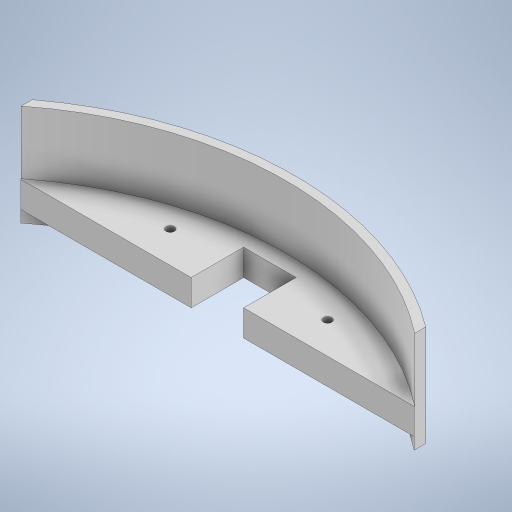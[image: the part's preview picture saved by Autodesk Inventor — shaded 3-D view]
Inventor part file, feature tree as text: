
AUTODESK INVENTOR PART (.ipt)
format: ipt  version: 2023 (Build 270158000, 158)  size: 374,784 bytes
history: native  units: mm
features: sketch x14, extrude x13, other x1, hole x1
ambient origin geometry x8: Origin, YZ Plane, XZ Plane, XY Plane, X Axis, Y Axis, Z Axis, Center Point
bodies: Body1 (feature_tree)
feature tree (29):
  other  "ソリッド1"
  extrude  "押し出し1"  Depth=250.0mm
  extrude  "押し出し2"  Depth=4.0mm TaperAngle=0.0deg
  sketch  "スケッチ4"
  extrude  "押し出し3"  Depth=150.0mm
  extrude  "押し出し4"  Depth=180.0mm
  extrude  "押し出し5"  Depth=243.0mm
  extrude  "押し出し6"  Depth=30.0mm TaperAngle=360.0deg
  extrude  "押し出し7"  Depth=10.0mm TaperAngle=0.0deg
  extrude  "押し出し8"  Depth=243.0mm
  extrude  "押し出し9"  Depth=243.0mm
  hole  "穴1"  [1 undecoded]
  extrude  "押し出し10"  Depth=30.0mm
  extrude  "押し出し11"  Depth=30.0mm
  extrude  "押し出し12"  Depth=10.0mm TaperAngle=0.0deg
  extrude  "押し出し13"  Depth=243.0mm
  sketch  "スケッチ1"
  sketch  "スケッチ2"
  sketch  "スケッチ5"
  sketch  "スケッチ6"
  sketch  "スケッチ7"
  sketch  "スケッチ8"
  sketch  "スケッチ9"
  sketch  "スケッチ12"
  sketch  "スケッチ13"
  sketch  "スケッチ14"
  sketch  "スケッチ15"
  sketch  "スケッチ16"
  sketch  "スケッチ17"
note: 1 required parameter value undecoded (feature->parameter linkage not recoverable at this tier; creation-order binding heuristic only, values carry confidence <= 0.55)
